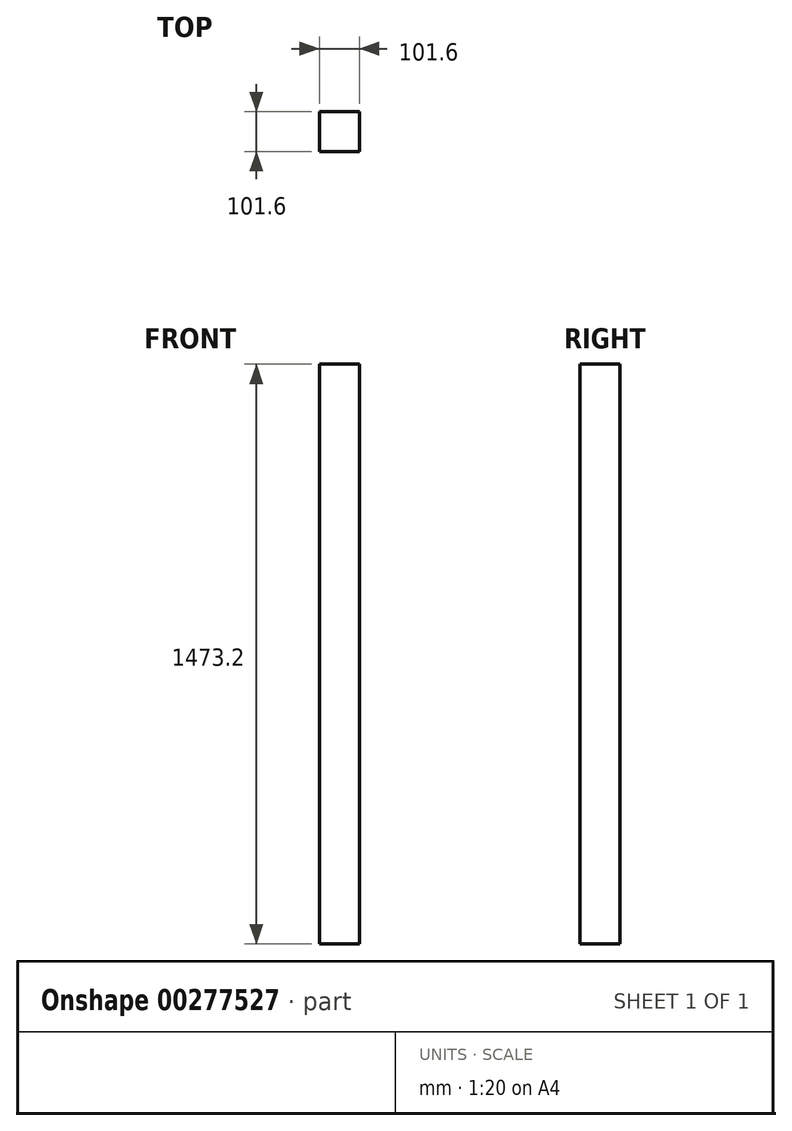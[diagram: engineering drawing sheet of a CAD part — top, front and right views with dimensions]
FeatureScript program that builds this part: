
annotation { "Feature Type Name" : "Feature", "Feature Type Description" : "" }
export const myFeature = defineFeature(function(context is Context, id is Id, definition is map)
    precondition{}
    {
        {
            var Q0;
            Q0=qCreatedBy(makeId("Top.planeOp"),FACE);
            var sketch = newSketch(context, id + "F0", { "sketchPlane" : qUnion([Q0])});
            skLineSegment(sketch, "E0.bottom", {"start": v(-50.8, 50.8) * mm, "end": v(50.8, 50.8) * mm});
            skLineSegment(sketch, "E0.top", {"start": v(-50.8, -50.8) * mm, "end": v(50.8, -50.8) * mm});
            skLineSegment(sketch, "E0.left", {"start": v(-50.8, 50.8) * mm, "end": v(-50.8, -50.8) * mm});
            skLineSegment(sketch, "E0.right", {"start": v(50.8, 50.8) * mm, "end": v(50.8, -50.8) * mm});
            skPoint(sketch, "E0.middle", {"position": v(0, 0) * mm});
            skSolve(sketch);
        }
        {
            var Q0;
            Q0=makeQuery(id+"F0.imprint","IMPRINT",FACE,{"disambiguationData":[TD([[makeQuery(id+"F0.imprint","IMPRINT",EDGE,{"derivedFrom":sQuery(id+"F0.wireOp",EDGE,"E0.bottom")}),-1.0]])]});
            extrude(context, id + "F1", {"entities" : qUnion([Q0]), "depth" : 1473.2 * mm});
        }
    });
